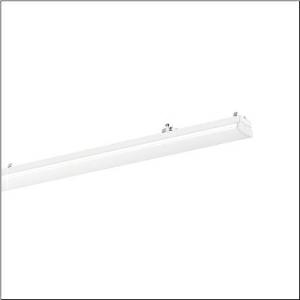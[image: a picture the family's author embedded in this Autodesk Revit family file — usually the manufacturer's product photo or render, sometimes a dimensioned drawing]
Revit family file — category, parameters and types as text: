
# Revit family: licross_21_recessed_opal_mo_52te1ddv4e5g
name_source: partatom
category: Lighting Fixtures
units: mm (PartAtom-declared; Revit-internal decimal feet)

## family parameters
Cut with Voids When Loaded = No
Host = Face
Light Source = No
Part Type = Normal
Room Calculation Point = No
Round Connector Dimension = Use Diameter
Shared = No

## types (1)
- --- (1 x LED, 14620 lm, 85.3 W, 4000K)
    Apparent Load = 85 VA
    CIE Flux Codes = 44 73 91 87 100
    Color Rendering = 80
    Color Temperature = 4000K
    Default Elevation = 1800 mm
    Description = Licross 21 recessed opal MO, luminaire insert, of sheet steel, galvanised, coil coated, white, length: 2.250mm, width: 66mm, height: 67mm, LED rated luminous flux: 14.620lm, light colour: 840, SDCM (Standard Deviation of Colour Matching)MacAdam ≤ 3 SDCM (initial), control gear: DALI 2, with plug, 5-pole, with phase selection, mains connection: 220..240V, AC, 50/60Hz, rated input power: 85W, internal wiring halogen-free, primary optical cover: cover, of PMMA, light emission: direct with ceiling illumination distribution, primary light characteristic: symmetric, protection rating (complete): IP54, insulation class (complete): insulation class I (protective earthing), certification: CE, ENEC, VDE, UKCA, protection symbol: D if used in an environment with non-conductive dust loads with corresponding accessories, impact resistance: IK06, permissible ambient temperature for indoor applications: -25..+35°C, corresponds to IFS (International Featured Standards) requirements for safety and quality in the food industry, reducing of maximum allowable ambient temperature of 5°C with ceiling mounting, LABS conformity tested according to VDMA 24364:2018-05, The light source and the operating device comply with the requirements of the Ecodesign Regulation (EU) 2019/2020 and are replaceable in accordance with this regulation, packaging unit: 1 piece
    Height = 83 mm
    Lamp = 1 x LED
    Lamp Light Flux = 14620 lm
    Lamp Power = 85.3 W
    Lamp count = 1
    Length = 2250 mm
    Luminous efficacy = 171 lm/W
    Manufacturer = Siteco
    ModVariant = No
    Model = 52TE1DDV4E5G
    Mounting Place = Ceiling
    Mounting Type = Pendant
    Number of Poles = 1
    OnlyDefault = Yes
    Power Factor = 1
    Product Name = Licross 21 recessed opal MO
    Product group = luminaire insert | ceiling pendant
    ProductGroupID = 901
    Protection Class = Protection class I
    Protection Degree = IP 54
    RLX_Detail_Level = 1
    RLX_Emergency_Light_Flux = 0 lm
    RLX_Emergency_Type = 0
    RLX_Emergency_Type_DB = No
    RlxData = <blob elided: 27057 chars, md5=4aba60b3>
    Socket = socket
    Standby Power = 0 W
    System Light Flux = 14620 lm
    System Power = 85 W
    Type Comments = factory setting: luminous flux: 100 % | dim-lin: 254 | 390 mA
    Type Image = l_1313666.jpg
    URL = http://relux.com
    VarID = @adj_072481
    Voltage = 0 V
    Weight = 0.00 kg
    Width = 76 mm

## geometry (parser evidence)
native form markers: Blend x4, Sweep x14
no freeform markers — native parametric forms only
